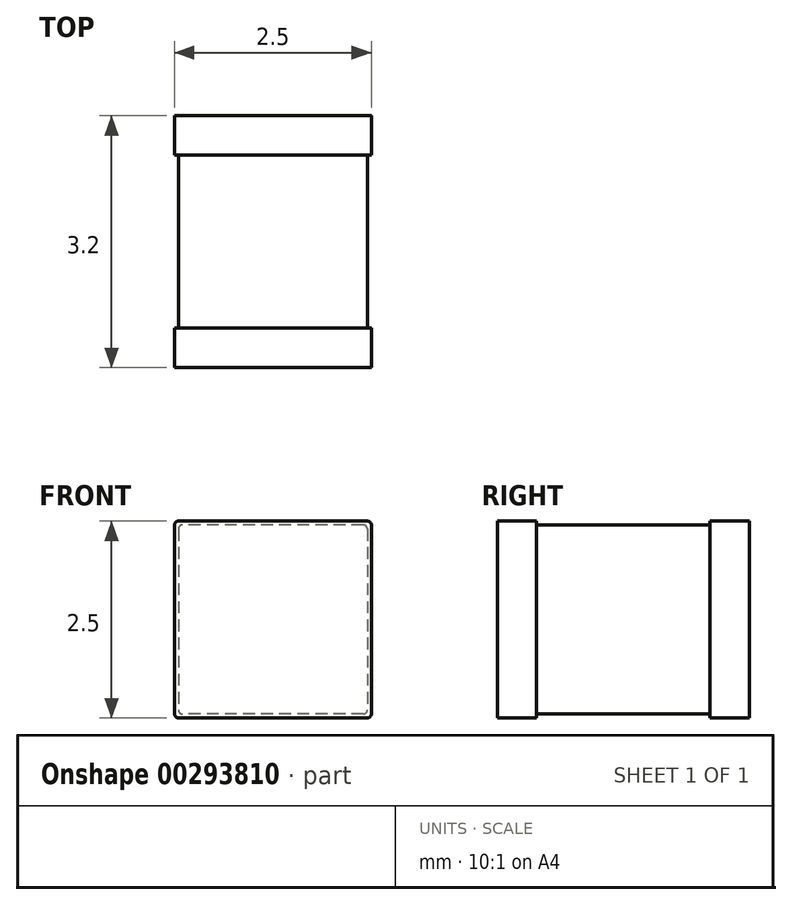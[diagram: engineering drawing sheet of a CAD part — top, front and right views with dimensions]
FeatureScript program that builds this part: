
annotation { "Feature Type Name" : "Feature", "Feature Type Description" : "" }
export const myFeature = defineFeature(function(context is Context, id is Id, definition is map)
    precondition{}
    {
        {
            var Q0;
            Q0=qCreatedBy(makeId("Front.planeOp"),FACE);
            var sketch = newSketch(context, id + "F0", { "sketchPlane" : qUnion([Q0])});
            skLineSegment(sketch, "E0.bottom", {"start": v(1.25, 1.25) * mm, "end": v(-1.25, 1.25) * mm});
            skLineSegment(sketch, "E0.top", {"start": v(1.25, -1.25) * mm, "end": v(-1.25, -1.25) * mm});
            skLineSegment(sketch, "E0.left", {"start": v(1.25, 1.25) * mm, "end": v(1.25, -1.25) * mm});
            skLineSegment(sketch, "E0.right", {"start": v(-1.25, 1.25) * mm, "end": v(-1.25, -1.25) * mm});
            skPoint(sketch, "E0.middle", {"position": v(0, 0) * mm});
            skSolve(sketch);
        }
        {
            var Q0;
            Q0 = qSketchRegion(id + "F0", true);
            extrude(context, id + "F1", {"entities" : qUnion([Q0]), "depth" : 0.5 * mm});
        }
        {
            var Q0;
            Q0=makeQuery(id+"F1.opExtrude","CAP_FACE",FACE,{"disambiguationData":[OSD([sQuery(id+"F0.wireOp",EDGE,"E0.bottom"),sQuery(id+"F0.wireOp",EDGE,"E0.top"),sQuery(id+"F0.wireOp",EDGE,"E0.left"),sQuery(id+"F0.wireOp",EDGE,"E0.right")])],"isStart":false});
            var sketch = newSketch(context, id + "F2", { "sketchPlane" : qUnion([Q0])});
            skLineSegment(sketch, "E1.bottom", {"start": v(1.2, 1.2) * mm, "end": v(-1.2, 1.2) * mm});
            skLineSegment(sketch, "E1.top", {"start": v(1.2, -1.2) * mm, "end": v(-1.2, -1.2) * mm});
            skLineSegment(sketch, "E1.left", {"start": v(1.2, 1.2) * mm, "end": v(1.2, -1.2) * mm});
            skLineSegment(sketch, "E1.right", {"start": v(-1.2, 1.2) * mm, "end": v(-1.2, -1.2) * mm});
            skPoint(sketch, "E1.middle", {"position": v(0, 0) * mm});
            skSolve(sketch);
        }
        {
            var Q0;
            Q0=makeQuery(id+"F2.imprint","IMPRINT",FACE,{"disambiguationData":[TD([[makeQuery(id+"F2.imprint","IMPRINT",EDGE,{"derivedFrom":sQuery(id+"F2.wireOp",EDGE,"E1.bottom")}),1.0]])]});
            extrude(context, id + "F3", {"entities" : qUnion([Q0]), "depth" : 2.2 * mm});
        }
        {
            var Q0;
            Q0=makeQuery(id+"F3.opExtrude","CAP_FACE",FACE,{"disambiguationData":[OSD([sQuery(id+"F2.wireOp",EDGE,"E1.bottom"),sQuery(id+"F2.wireOp",EDGE,"E1.top"),sQuery(id+"F2.wireOp",EDGE,"E1.left"),sQuery(id+"F2.wireOp",EDGE,"E1.right")])],"isStart":false});
            var sketch = newSketch(context, id + "F4", { "sketchPlane" : qUnion([Q0])});
            skLineSegment(sketch, "E2.bottom", {"start": v(1.25, 1.25) * mm, "end": v(-1.25, 1.25) * mm});
            skLineSegment(sketch, "E2.top", {"start": v(1.25, -1.25) * mm, "end": v(-1.25, -1.25) * mm});
            skLineSegment(sketch, "E2.left", {"start": v(1.25, 1.25) * mm, "end": v(1.25, -1.25) * mm});
            skLineSegment(sketch, "E2.right", {"start": v(-1.25, 1.25) * mm, "end": v(-1.25, -1.25) * mm});
            skPoint(sketch, "E2.middle", {"position": v(0, 0) * mm});
            skSolve(sketch);
        }
        {
            var Q0;
            Q0 = qSketchRegion(id + "F4", true);
            extrude(context, id + "F5", {"entities" : qUnion([Q0]), "depth" : 0.5 * mm});
        }
        {
            var Q0;
            Q0=makeQuery(id+"F5.opExtrude","SWEPT_EDGE",EDGE,{"disambiguationData":[OSD([sQuery(id+"F4.wireOp",EDGE,"E2.bottom"),sQuery(id+"F4.wireOp",EDGE,"E2.left")])]});
            var Q1;
            Q1=makeQuery(id+"F5.opExtrude","SWEPT_EDGE",EDGE,{"disambiguationData":[OSD([sQuery(id+"F4.wireOp",EDGE,"E2.top"),sQuery(id+"F4.wireOp",EDGE,"E2.left")])]});
            var Q2;
            Q2=makeQuery(id+"F1.opExtrude","SWEPT_EDGE",EDGE,{"disambiguationData":[OSD([sQuery(id+"F0.wireOp",EDGE,"E0.bottom"),sQuery(id+"F0.wireOp",EDGE,"E0.left")])]});
            var Q3;
            Q3=makeQuery(id+"F1.opExtrude","SWEPT_EDGE",EDGE,{"disambiguationData":[OSD([sQuery(id+"F0.wireOp",EDGE,"E0.top"),sQuery(id+"F0.wireOp",EDGE,"E0.left")])]});
            var Q4;
            Q4=makeQuery(id+"F3.opExtrude","SWEPT_EDGE",EDGE,{"disambiguationData":[OSD([sQuery(id+"F2.wireOp",EDGE,"E1.bottom"),sQuery(id+"F2.wireOp",EDGE,"E1.left")])]});
            var Q5;
            Q5=makeQuery(id+"F1.opExtrude","SWEPT_EDGE",EDGE,{"disambiguationData":[OSD([sQuery(id+"F0.wireOp",EDGE,"E0.bottom"),sQuery(id+"F0.wireOp",EDGE,"E0.right")])]});
            var Q6;
            Q6=makeQuery(id+"F3.opExtrude","SWEPT_EDGE",EDGE,{"disambiguationData":[OSD([sQuery(id+"F2.wireOp",EDGE,"E1.bottom"),sQuery(id+"F2.wireOp",EDGE,"E1.right")])]});
            var Q7;
            Q7=makeQuery(id+"F5.opExtrude","SWEPT_EDGE",EDGE,{"disambiguationData":[OSD([sQuery(id+"F4.wireOp",EDGE,"E2.bottom"),sQuery(id+"F4.wireOp",EDGE,"E2.right")])]});
            var Q8;
            Q8=makeQuery(id+"F3.opExtrude","SWEPT_EDGE",EDGE,{"disambiguationData":[OSD([sQuery(id+"F2.wireOp",EDGE,"E1.top"),sQuery(id+"F2.wireOp",EDGE,"E1.left")])]});
            var Q9;
            Q9=makeQuery(id+"F3.opExtrude","SWEPT_EDGE",EDGE,{"disambiguationData":[OSD([sQuery(id+"F2.wireOp",EDGE,"E1.top"),sQuery(id+"F2.wireOp",EDGE,"E1.right")])]});
            var Q10;
            Q10=makeQuery(id+"F5.opExtrude","SWEPT_EDGE",EDGE,{"disambiguationData":[OSD([sQuery(id+"F4.wireOp",EDGE,"E2.top"),sQuery(id+"F4.wireOp",EDGE,"E2.right")])]});
            var Q11;
            Q11=makeQuery(id+"F1.opExtrude","SWEPT_EDGE",EDGE,{"disambiguationData":[OSD([sQuery(id+"F0.wireOp",EDGE,"E0.top"),sQuery(id+"F0.wireOp",EDGE,"E0.right")])]});
            fillet(context, id + "F6", {"entities" : qUnion([Q0, Q1, Q2, Q3, Q4, Q5, Q6, Q7, Q8, Q9, Q10, Q11]), "radius" : 0.05 * mm, "tangentPropagation" : true, "allowEdgeOverflow" : false});
        }
    });
